# Revit family: CirLED Wall - Wall based
name_source: partatom
category: Lighting Fixtures
revit_build: Autodesk Revit Architecture 2014 (Build: 20140709_2115(x64)
units: mm (PartAtom-declared; Revit-internal decimal feet)

## types (1)
- CircLED Wall
    Apparent Load = 240 VA
    ArticleNumber = See URL hyperlink
    AssetType = Moveable/Fixed
    BIMObjectName = CircLED Wall.rfa
    BSAB 96 = SNB.2
    BallastsCELMAEnergyEfficiencyIndex = Class A1/A2
    CCSClassCode = UAC
    CCSClassName = Belysningsarmatur
    CCSTopnode = L
    Color Filter = 16777215
    Colour = Grey / Black
    ControlGearPosition = Integrated
    Description = 70-80-35 General Lighting Systems
    Dimming Lamp Color Temperature Shift = <None>
    DocumentReference = See URL hyperlink
    Documentation = See URL hyperlink
    Finish = Powder coated
    Frame = Riegens_Aluminum_powder coated grey
    Frame Depth = 460 mm
    Frame Thickness = 185 mm
    Frame Width = 390 mm
    HasProtectiveEarth = TRUE
    IP_Code = IP54
    IfcExportAs = IfcLightFixtureType'
    IfcExportType = NOTDEFINED'
    InsulationStandardClass = Class 1
    InternalFuse = Only required in emergency versions
    LampColourRenderingIndex = Ra>80
    LampRating = 17W / 19W
    LampType = LED
    LightFixtureMountingType = Wall
    LightFixturePlacingType = Wall
    LightSource = LED 4000K
    LuminairePowerFactor = >0,9
    LuminaireType = Outdoor Direct LED Luminaire
    Manufacturer = Riegens A/S
    ManufacturerURL = www.riegens.com
    Material = Aluminium, plastic and glass.
    Model = CircLED Wall
    ModelReference = CircLED Wall
    NominalVoltage = 220-240V
    Optic = Clear front and lens S / lens M
    PhaseReference = IEC recommendations
    Photometric Web File = CircLED MultiLens 19W 4000K Glas.ies
    PhotometricPerformance = In accordance with BS EN 13032-1
    ProductInformation = http://riegens.com
    Shape = Oval
    Size = 460 x 390 mm
    Tilt Angle = 90.00°
    TotalWattage = 17W / 19W
    URL = http://riegens.com
    Uniclass 1.4 = JY73
    Uniclass2 = Pr_70_70_49_43 Light-Emitting Diode (LED) Luminaires
    Version = v.1.0

## geometry (parser evidence)
native form markers: Sweep x2
no freeform markers — native parametric forms only
